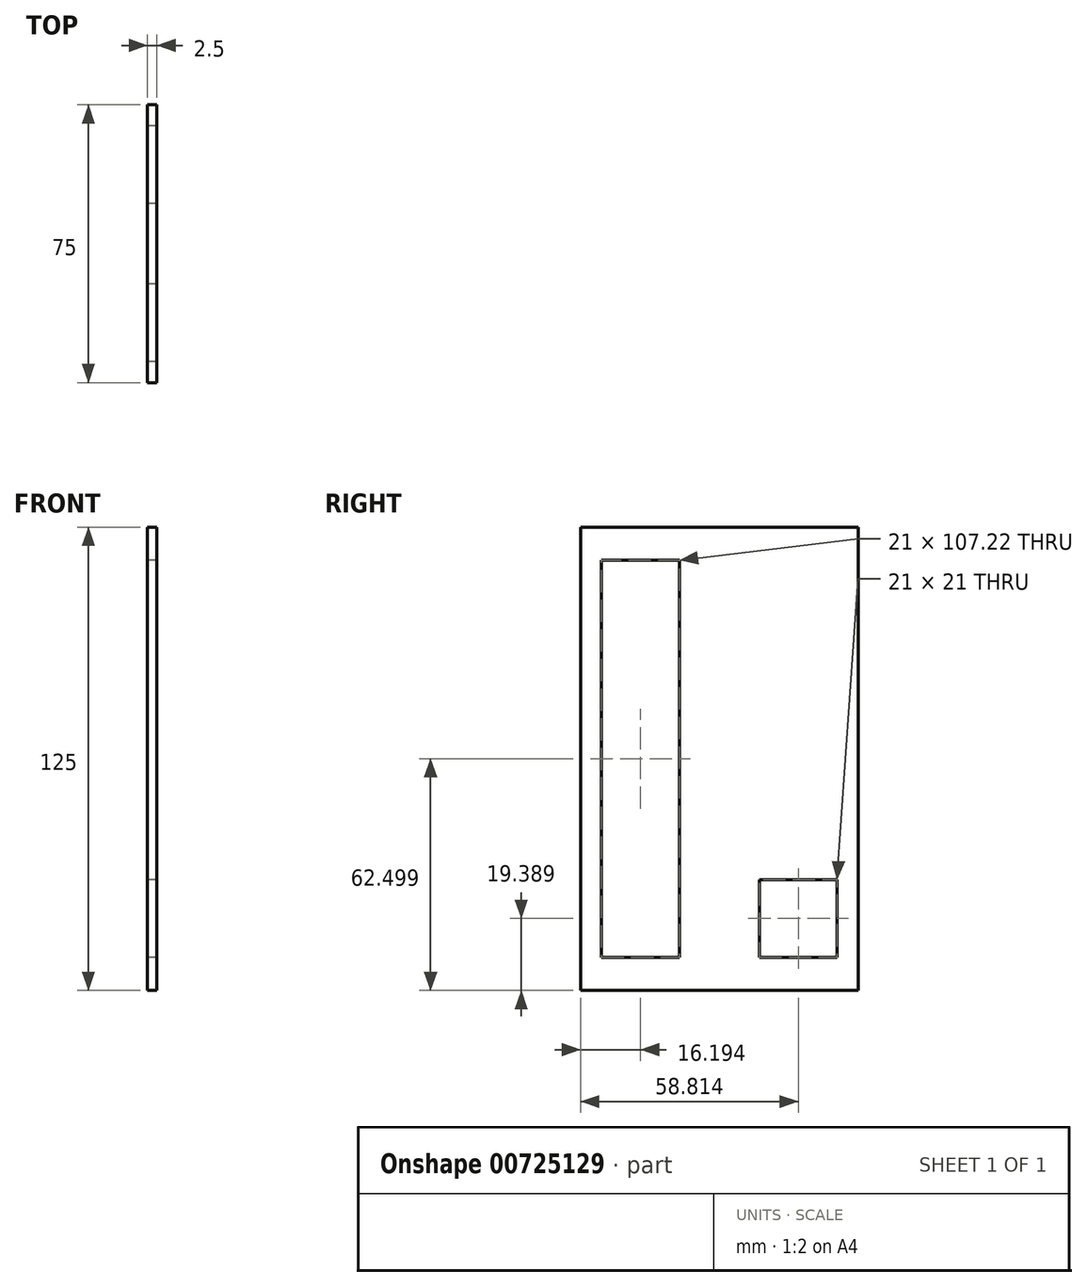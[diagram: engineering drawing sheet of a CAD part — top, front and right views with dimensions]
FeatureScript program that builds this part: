
annotation { "Feature Type Name" : "Feature", "Feature Type Description" : "" }
export const myFeature = defineFeature(function(context is Context, id is Id, definition is map)
    precondition{}
    {
        {
            var Q0;
            Q0=qCreatedBy(makeId("Right.planeOp"),FACE);
            var sketch = newSketch(context, id + "F0", { "sketchPlane" : qUnion([Q0])});
            skLineSegment(sketch, "E0.bottom", {"start": v(4.28, 15.8) * mm, "end": v(79.28, 15.8) * mm});
            skLineSegment(sketch, "E0.left", {"start": v(4.28, 15.8) * mm, "end": v(4.28, 140.8) * mm});
            skLineSegment(sketch, "E1.top", {"start": v(8.1, 19.62) * mm, "end": v(75.47, 19.62) * mm});
            skLineSegment(sketch, "E1.left", {"start": v(8.1, 137) * mm, "end": v(8.1, 19.62) * mm});
            skLineSegment(sketch, "E2.bottom", {"start": v(4.28, 140.8) * mm, "end": v(55.8, 140.8) * mm});
            skLineSegment(sketch, "E2.top", {"start": v(11.3, 140.8) * mm, "end": v(55.8, 140.8) * mm});
            skLineSegment(sketch, "E2.left", {"start": v(-20.61, 45.23) * mm, "end": v(-20.61, 45.23) * mm});
            skLineSegment(sketch, "E3", {"start": v(8.1, 137) * mm, "end": v(55.8, 137) * mm});
            skLineSegment(sketch, "E4", {"start": v(61.48, 137) * mm, "end": v(61.48, 140.8) * mm});
            skLineSegment(sketch, "E5", {"start": v(55.8, 140.8) * mm, "end": v(61.48, 140.8) * mm});
            skLineSegment(sketch, "E6", {"start": v(61.48, 137) * mm, "end": v(55.8, 137) * mm});
            skLineSegment(sketch, "E7", {"start": v(75.47, 19.62) * mm, "end": v(75.47, 140.8) * mm});
            skLineSegment(sketch, "E8", {"start": v(75.47, 140.8) * mm, "end": v(79.28, 140.8) * mm});
            skLineSegment(sketch, "E9", {"start": v(79.28, 140.8) * mm, "end": v(79.28, 15.8) * mm});
            skLineSegment(sketch, "E10", {"start": v(61.48, 137) * mm, "end": v(75.47, 137) * mm});
            skLineSegment(sketch, "E11", {"start": v(75.47, 137) * mm, "end": v(75.47, 140.8) * mm});
            skLineSegment(sketch, "E12", {"start": v(61.48, 140.8) * mm, "end": v(75.47, 140.8) * mm});
            skLineSegment(sketch, "E13", {"start": v(9.97, 131.92) * mm, "end": v(9.97, 24.7) * mm});
            skLineSegment(sketch, "E14", {"start": v(9.97, 24.7) * mm, "end": v(30.97, 24.7) * mm});
            skLineSegment(sketch, "E15", {"start": v(30.97, 24.7) * mm, "end": v(30.97, 110.92) * mm});
            skLineSegment(sketch, "E16", {"start": v(52.6, 24.7) * mm, "end": v(73.6, 24.7) * mm});
            skLineSegment(sketch, "E17", {"start": v(73.6, 24.7) * mm, "end": v(73.6, 131.92) * mm});
            skLineSegment(sketch, "E18", {"start": v(73.6, 131.92) * mm, "end": v(52.6, 131.92) * mm});
            skLineSegment(sketch, "E19", {"start": v(52.6, 131.92) * mm, "end": v(52.6, 131.92) * mm});
            skLineSegment(sketch, "E20", {"start": v(52.6, 131.92) * mm, "end": v(30.97, 131.92) * mm});
            skLineSegment(sketch, "E21", {"start": v(30.97, 131.92) * mm, "end": v(30.97, 131.92) * mm});
            skLineSegment(sketch, "E22", {"start": v(30.97, 131.92) * mm, "end": v(9.97, 131.92) * mm});
            skLineSegment(sketch, "E23", {"start": v(52.6, 24.7) * mm, "end": v(52.6, 45.7) * mm});
            skLineSegment(sketch, "E24", {"start": v(9.97, 45.7) * mm, "end": v(30.97, 45.7) * mm});
            skLineSegment(sketch, "E25", {"start": v(52.6, 45.7) * mm, "end": v(73.6, 45.7) * mm});
            skLineSegment(sketch, "E26", {"start": v(73.6, 45.7) * mm, "end": v(73.6, 49.5) * mm});
            skLineSegment(sketch, "E27", {"start": v(30.97, 110.92) * mm, "end": v(30.97, 131.92) * mm});
            skSolve(sketch);
        }
        {
            var Q0;
            {var subQ0=makeQuery(id+"F0.imprint","IMPRINT",EDGE,{"derivedFrom":sQuery(id+"F0.wireOp",EDGE,"E4")});Q0=qUnion([makeQuery(id+"F0.imprint","IMPRINT",FACE,{"disambiguationData":[TD([[makeQuery(id+"F0.imprint","IMPRINT",EDGE,{"derivedFrom":sQuery(id+"F0.wireOp",EDGE,"E0.bottom")}),1.0]])]}),makeQuery(id+"F0.imprint","IMPRINT",FACE,{"disambiguationData":[TD([[subQ0,-1.0]])]})]);}
            var Q1;
            {var subQ9=sQuery(id+"F0.wireOp",EDGE,"E1.top");Q1=makeQuery(id+"F0.imprint","IMPRINT",FACE,{"disambiguationData":[TD([[makeQuery(id+"F0.imprint","IMPRINT",EDGE,{"derivedFrom":subQ9}),1.0]])]});}
            var Q2;
            {var subQ0=sQuery(id+"F0.wireOp",EDGE,"JLpqCohK-HEtu-8vcU-U4sc-vSC7FxLXl771");Q2=makeQuery(id+"F0.imprint","IMPRINT",FACE,{"disambiguationData":[TD([[makeQuery(id+"F0.imprint","IMPRINT",EDGE,{"derivedFrom":subQ0}),1.0]])]});}
            var Q3;
            {var subQ0=sQuery(id+"F0.wireOp",EDGE,"ONWxT9Oq-NQbA-cWWp-UdgU-v9UcCOu7any3");Q3=makeQuery(id+"F0.imprint","IMPRINT",FACE,{"disambiguationData":[TD([[makeQuery(id+"F0.imprint","IMPRINT",EDGE,{"derivedFrom":subQ0}),1.0]])]});}
            var Q4;
            {var subQ0=sQuery(id+"F0.wireOp",EDGE,"HAdENxz2-tm0k-my0M-ARQP-1q9sxu4kPaf8");Q4=makeQuery(id+"F0.imprint","IMPRINT",FACE,{"disambiguationData":[TD([[makeQuery(id+"F0.imprint","IMPRINT",EDGE,{"derivedFrom":subQ0}),1.0]])]});}
            var Q5;
            {var subQ0=sQuery(id+"F0.wireOp",EDGE,"ZU0bbuyQ-MHcU-MSQz-OdO2-vLknINNZd6GF");Q5=makeQuery(id+"F0.imprint","IMPRINT",FACE,{"disambiguationData":[TD([[makeQuery(id+"F0.imprint","IMPRINT",EDGE,{"derivedFrom":subQ0}),1.0]])]});}
            var Q6;
            {var subQ9=sQuery(id+"F0.wireOp",EDGE,"E1.top");Q6=makeQuery(id+"F0.imprint","IMPRINT",FACE,{"disambiguationData":[TD([[makeQuery(id+"F0.imprint","IMPRINT",EDGE,{"derivedFrom":subQ9}),1.0]])]});}
            var Q7;
            {var subQ1=sQuery(id+"F0.wireOp",EDGE,"pWInZMHu-sZtc-m760-aJ1d-ciON90ufgcsd");Q7=makeQuery(id+"F0.imprint","IMPRINT",FACE,{"disambiguationData":[TD([[makeQuery(id+"F0.imprint","IMPRINT",EDGE,{"derivedFrom":subQ1}),-1.0]])]});}
            var Q8;
            {var subQ4=sQuery(id+"F0.wireOp",EDGE,"NGl3fMWX-xWQt-SUei-zx6P-FE3a8lybHdwg");Q8=makeQuery(id+"F0.imprint","IMPRINT",FACE,{"disambiguationData":[TD([[makeQuery(id+"F0.imprint","IMPRINT",EDGE,{"derivedFrom":subQ4}),-1.0]])]});}
            extrude(context, id + "F1", {"entities" : qUnion([Q0, Q1, Q2, Q3, Q4, Q5, Q6, Q7, Q8]), "depth" : 2.5 * mm, "offsetDistance" : 25.4 * mm});
        }
    });
